# Revit family: 5041xxx Curve Glass 285
name_source: partatom
category: Lighting Fixtures
units: mm (PartAtom-declared; Revit-internal decimal feet)

## family parameters
Always vertical = Yes
Cut with Voids When Loaded = No
Host = Ceiling
Light Source = No
Maintain Annotation Orientation = No
OmniClass Number = 23.80.70.11
OmniClass Title = Luminaries for Internal Lighting
Part Type = Normal
Room Calculation Point = No
Round Connector Dimension = Use Diameter
Shared = No

## types (2) — shared parameters
Manufacturer URL - Europe and Rest of World = www.astrolighting.com
Manufacturer URL - North America = us.astrolighting.com
zero-valued in all types: Default Elevation, Product Weight (KG)

## per-type parameters (varying)
| type | Main Finish | Main Material | Product CCT | Product CRI | Product Dimensions (MM) | Product Name | Product SKU |
| CE |  |  | 2700K / 3000K | 80 / 90 |  |  | 1234567 |
| ETL | Dark Smoke | Glass |  |  | 287 x 240 | Curve Glass 285 | 5041002 |

## geometry (parser evidence)
native form markers: Sweep x3
no freeform markers — native parametric forms only
